annotation { "Feature Type Name" : "Feature", "Feature Type Description" : "" }
export const myFeature = defineFeature(function(context is Context, id is Id, definition is map)
    precondition{}
    {
        {
            var Q0;
            Q0=qCreatedBy(makeId("Top.planeOp"),FACE);
            cPlane(context, id + "F0", {"entities" : qUnion([Q0]), "cplaneType" : CPlaneType.OFFSET, "offset" : 2.5 * mm, "width" : 150 * mm, "height" : 150 * mm});
        }
        {
            var Q0;
            Q0=qCreatedBy(id+"F0.planeOp",FACE);
            var sketch = newSketch(context, id + "F1", { "sketchPlane" : qUnion([Q0])});
            skLineSegment(sketch, "E0.bottom", {"start": v(60, -25) * mm, "end": v(-60, -25) * mm});
            skLineSegment(sketch, "E0.top", {"start": v(60, 25) * mm, "end": v(-60, 25) * mm});
            skLineSegment(sketch, "E0.left", {"start": v(65, -20) * mm, "end": v(65, 20) * mm});
            skLineSegment(sketch, "E0.right", {"start": v(-65, -20) * mm, "end": v(-65, 20) * mm});
            skPoint(sketch, "E0.middle", {"position": v(0, 0) * mm});
            skPoint(sketch, "E1.visualSharp", {"position": v(-65, 25) * mm});
            skArc(sketch, "E1.filletArc", {"start": v(-60, 25) * mm, "mid": v(-63.54, 23.54) * mm, "end": v(-65, 20) * mm});
            skPoint(sketch, "E2.visualSharp", {"position": v(65, 25) * mm});
            skArc(sketch, "E2.filletArc", {"start": v(65, 20) * mm, "mid": v(63.54, 23.54) * mm, "end": v(60, 25) * mm});
            skPoint(sketch, "E3.visualSharp", {"position": v(65, -25) * mm});
            skArc(sketch, "E3.filletArc", {"start": v(60, -25) * mm, "mid": v(63.54, -23.54) * mm, "end": v(65, -20) * mm});
            skPoint(sketch, "E4.visualSharp", {"position": v(-65, -25) * mm});
            skArc(sketch, "E4.filletArc", {"start": v(-65, -20) * mm, "mid": v(-63.54, -23.54) * mm, "end": v(-60, -25) * mm});
            skSolve(sketch);
        }
        {
            var Q0;
            Q0=qSketchRegion(id+"F1",true);
            extrude(context, id + "F2", {"entities" : qUnion([Q0]), "depth" : 1 * mm, "offsetDistance" : 25 * mm});
        }
        {
            var Q0;
            Q0=qCreatedBy(makeId("Top.planeOp"),FACE);
            var sketch = newSketch(context, id + "F3", { "sketchPlane" : qUnion([Q0])});
            skCircle(sketch, "E5", {"center": v(0, 0) * mm, "radius": 5 * mm});
            skSolve(sketch);
        }
        {
            var Q0;
            Q0 = qSketchRegion(id + "F3", true);
            extrude(context, id + "F4", {"entities" : qUnion([Q0]), "operationType" : NewBodyOperationType.ADD, "depth" : 2.5 * mm, "offsetDistance" : 25 * mm});
        }
        {
            var Q0;
            Q0=makeQuery(id+"F2.opExtrude","CAP_FACE",FACE,{"disambiguationData":[OSD([sQuery(id+"F1.wireOp",EDGE,"E0.bottom"),sQuery(id+"F1.wireOp",EDGE,"E0.top"),sQuery(id+"F1.wireOp",EDGE,"E0.left"),sQuery(id+"F1.wireOp",EDGE,"E0.right"),sQuery(id+"F1.wireOp",EDGE,"E1.filletArc"),sQuery(id+"F1.wireOp",EDGE,"E2.filletArc"),sQuery(id+"F1.wireOp",EDGE,"E3.filletArc"),sQuery(id+"F1.wireOp",EDGE,"E4.filletArc")])],"isStart":false});
            var sketch = newSketch(context, id + "F5", { "sketchPlane" : qUnion([Q0])});
            skLineSegment(sketch, "E6.bottom", {"start": v(60, -25) * mm, "end": v(-60, -25) * mm});
            skLineSegment(sketch, "E6.top", {"start": v(60, 25) * mm, "end": v(-60, 25) * mm});
            skLineSegment(sketch, "E6.left", {"start": v(65, -20) * mm, "end": v(65, 20) * mm});
            skLineSegment(sketch, "E6.right", {"start": v(-65, -20) * mm, "end": v(-65, 20) * mm});
            skPoint(sketch, "E6.middle", {"position": v(0, 0) * mm});
            skLineSegment(sketch, "E7.bottom", {"start": v(60, -22) * mm, "end": v(-60, -22) * mm});
            skLineSegment(sketch, "E7.top", {"start": v(60, 22) * mm, "end": v(-60, 22) * mm});
            skLineSegment(sketch, "E7.left", {"start": v(62, -20) * mm, "end": v(62, 20) * mm});
            skLineSegment(sketch, "E7.right", {"start": v(-62, -20) * mm, "end": v(-62, 20) * mm});
            skPoint(sketch, "E8.visualSharp", {"position": v(-62, 22) * mm});
            skArc(sketch, "E8.filletArc", {"start": v(-60, 22) * mm, "mid": v(-61.41, 21.41) * mm, "end": v(-62, 20) * mm});
            skPoint(sketch, "E9.visualSharp", {"position": v(62, 22) * mm});
            skArc(sketch, "E9.filletArc", {"start": v(62, 20) * mm, "mid": v(61.41, 21.41) * mm, "end": v(60, 22) * mm});
            skPoint(sketch, "E10.visualSharp", {"position": v(62, -22) * mm});
            skArc(sketch, "E10.filletArc", {"start": v(60, -22) * mm, "mid": v(61.41, -21.41) * mm, "end": v(62, -20) * mm});
            skPoint(sketch, "E11.visualSharp", {"position": v(-62, -22) * mm});
            skArc(sketch, "E11.filletArc", {"start": v(-62, -20) * mm, "mid": v(-61.41, -21.41) * mm, "end": v(-60, -22) * mm});
            skPoint(sketch, "E12.visualSharp", {"position": v(-65, 25) * mm});
            skArc(sketch, "E12.filletArc", {"start": v(-60, 25) * mm, "mid": v(-63.54, 23.54) * mm, "end": v(-65, 20) * mm});
            skPoint(sketch, "E13.visualSharp", {"position": v(65, 25) * mm});
            skArc(sketch, "E13.filletArc", {"start": v(65, 20) * mm, "mid": v(63.54, 23.54) * mm, "end": v(60, 25) * mm});
            skPoint(sketch, "E14.visualSharp", {"position": v(65, -25) * mm});
            skArc(sketch, "E14.filletArc", {"start": v(60, -25) * mm, "mid": v(63.54, -23.54) * mm, "end": v(65, -20) * mm});
            skPoint(sketch, "E15.visualSharp", {"position": v(-65, -25) * mm});
            skArc(sketch, "E15.filletArc", {"start": v(-65, -20) * mm, "mid": v(-63.54, -23.54) * mm, "end": v(-60, -25) * mm});
            skSolve(sketch);
        }
        {
            var Q0;
            Q0 = qSketchRegion(id + "F5", true);
            extrude(context, id + "F6", {"entities" : qUnion([Q0]), "operationType" : NewBodyOperationType.ADD, "depth" : 2 * mm, "offsetDistance" : 25 * mm});
        }
        {
            var Q0;
            Q0=makeQuery(id+"F2.opExtrude","CAP_FACE",FACE,{"disambiguationData":[OSD([sQuery(id+"F1.wireOp",EDGE,"E0.bottom"),sQuery(id+"F1.wireOp",EDGE,"E0.top"),sQuery(id+"F1.wireOp",EDGE,"E0.left"),sQuery(id+"F1.wireOp",EDGE,"E0.right"),sQuery(id+"F1.wireOp",EDGE,"E1.filletArc"),sQuery(id+"F1.wireOp",EDGE,"E2.filletArc"),sQuery(id+"F1.wireOp",EDGE,"E3.filletArc"),sQuery(id+"F1.wireOp",EDGE,"E4.filletArc")])],"isStart":false});
            var sketch = newSketch(context, id + "F7", { "sketchPlane" : qUnion([Q0])});
            skCircle(sketch, "E16", {"center": v(-25, 0) * mm, "radius": 5 * mm});
            skCircle(sketch, "E17", {"center": v(25, 0) * mm, "radius": 5 * mm});
            skSolve(sketch);
        }
        {
            var Q0;
            Q0 = qSketchRegion(id + "F7", true);
            extrude(context, id + "F8", {"entities" : qUnion([Q0]), "operationType" : NewBodyOperationType.REMOVE, "oppositeDirection" : true, "depth" : 1 * mm, "offsetDistance" : 25 * mm});
        }
        {
            var Q0;
            Q0=qCreatedBy(makeId("Top.planeOp"),FACE);
            cPlane(context, id + "F9", {"entities" : qUnion([Q0]), "cplaneType" : CPlaneType.OFFSET, "offset" : 3.5 * mm, "width" : 150 * mm, "height" : 150 * mm});
        }
        {
            var Q0;
            Q0=qCreatedBy(id+"F9.planeOp",FACE);
            var sketch = newSketch(context, id + "F10", { "sketchPlane" : qUnion([Q0])});
            skText(sketch, "E18", { "text": "JOY RIDE", "fontName": "RobotoSlab-Bold.ttf"});
            const initialGuessF10  = {"E18": [-0.06, -0.00981, 1, 0, 0.01881]};
            skSetInitialGuess(sketch, initialGuessF10);
            skSolve(sketch);
        }
        {
            var Q0;
            Q0 = qSketchRegion(id + "F10", true);
            extrude(context, id + "F11", {"entities" : qUnion([Q0]), "operationType" : NewBodyOperationType.ADD, "depth" : 2 * mm, "offsetDistance" : 25 * mm});
        }
    });